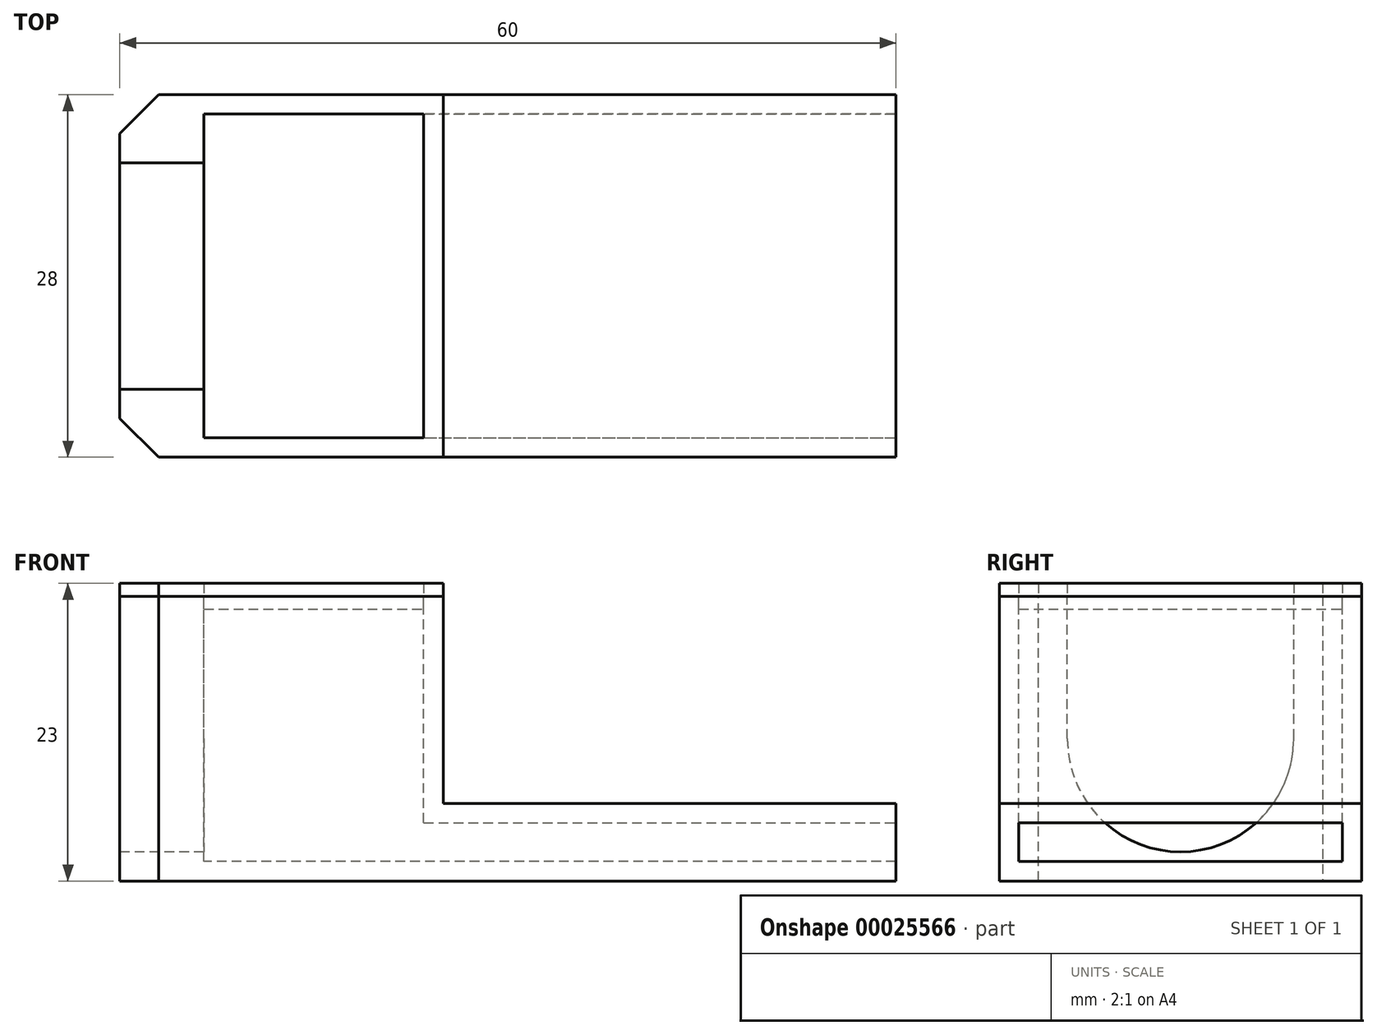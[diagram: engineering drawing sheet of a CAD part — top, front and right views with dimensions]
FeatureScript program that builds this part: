
annotation { "Feature Type Name" : "Feature", "Feature Type Description" : "" }
export const myFeature = defineFeature(function(context is Context, id is Id, definition is map)
    precondition{}
    {
        {
            var Q0;
            Q0=qCreatedBy(makeId("Front.planeOp"),FACE);
            var sketch = newSketch(context, id + "F0", { "sketchPlane" : qUnion([Q0])});
            skLineSegment(sketch, "E0", {"start": v(0, 0) * mm, "end": v(55, 0) * mm});
            skLineSegment(sketch, "E1", {"start": v(0, 0) * mm, "end": v(0, 22) * mm});
            skLineSegment(sketch, "E2", {"start": v(0, 22) * mm, "end": v(20, 22) * mm});
            skLineSegment(sketch, "E3", {"start": v(20, 22) * mm, "end": v(20, 6) * mm});
            skLineSegment(sketch, "E4", {"start": v(20, 6) * mm, "end": v(55, 6) * mm});
            skLineSegment(sketch, "E5", {"start": v(55, 6) * mm, "end": v(55, 0) * mm});
            skSolve(sketch);
        }
        {
            var Q0;
            Q0 = qSketchRegion(id + "F0", true);
            extrude(context, id + "F1", {"entities" : qUnion([Q0]), "depth" : 28 * mm});
        }
        {
            var Q0;
            Q0=makeQuery(id+"F1.opExtrude","SWEPT_FACE",FACE,{"disambiguationData":[OSD([sQuery(id+"F0.wireOp",EDGE,"E1")])]});
            var sketch = newSketch(context, id + "F2", { "sketchPlane" : qUnion([Q0])});
            skArc(sketch, "E6", {"start": v(5.25, 11) * mm, "mid": v(14, 2.25) * mm, "end": v(22.75, 11) * mm});
            skPoint(sketch, "E6.centerSnap0", {"position": v(28, 11) * mm});
            skPoint(sketch, "E6.centerSnap1", {"position": v(14, 22) * mm});
            skLineSegment(sketch, "E7", {"start": v(5.25, 11) * mm, "end": v(5.25, 22) * mm});
            skLineSegment(sketch, "E8", {"start": v(22.75, 11) * mm, "end": v(22.75, 22) * mm});
            skSolve(sketch);
        }
        {
            var Q0;
            Q0=makeQuery(id+"F1.opExtrude","SWEPT_FACE",FACE,{"disambiguationData":[OSD([sQuery(id+"F0.wireOp",EDGE,"E2")])]});
            var sketch = newSketch(context, id + "F3", { "sketchPlane" : qUnion([Q0])});
            skLineSegment(sketch, "E9.0", {"start": v(18.5, -1.5) * mm, "end": v(1.5, -1.5) * mm});
            skLineSegment(sketch, "E9.1", {"start": v(18.5, -26.5) * mm, "end": v(18.5, -1.5) * mm});
            skLineSegment(sketch, "E9.2", {"start": v(1.5, -26.5) * mm, "end": v(18.5, -26.5) * mm});
            skLineSegment(sketch, "E9.3", {"start": v(1.5, -1.5) * mm, "end": v(1.5, -26.5) * mm});
            skSolve(sketch);
        }
        {
            var Q0;
            Q0=makeQuery(id+"F3.imprint","IMPRINT",FACE,{"disambiguationData":[TD([[makeQuery(id+"F3.imprint","IMPRINT",EDGE,{"derivedFrom":sQuery(id+"F3.wireOp",EDGE,"E9.0")}),1.0]])]});
            extrude(context, id + "F4", {"entities" : qUnion([Q0]), "operationType" : NewBodyOperationType.REMOVE, "oppositeDirection" : true, "depth" : 20.5 * mm});
        }
        {
            var Q0;
            Q0 = qSketchRegion(id + "F2", true);
            var Q1;
            Q1=makeQuery(id+"F2.imprint","IMPRINT",FACE,{"disambiguationData":[TD([[makeQuery(id+"F2.imprint","IMPRINT",EDGE,{"derivedFrom":sQuery(id+"F2.wireOp",EDGE,"E6")}),1.0]])]});
            extrude(context, id + "F5", {"entities" : qUnion([Q0, Q1]), "operationType" : NewBodyOperationType.REMOVE, "oppositeDirection" : true, "depth" : 2 * mm});
        }
        {
            var Q0;
            Q0=makeQuery(id+"F1.opExtrude","SWEPT_FACE",FACE,{"disambiguationData":[OSD([sQuery(id+"F0.wireOp",EDGE,"E5")])]});
            var sketch = newSketch(context, id + "F6", { "sketchPlane" : qUnion([Q0])});
            skLineSegment(sketch, "E10.0", {"start": v(-1.5, 1.5) * mm, "end": v(-1.5, 4.5) * mm});
            skLineSegment(sketch, "E10.1", {"start": v(-26.5, 1.5) * mm, "end": v(-1.5, 1.5) * mm});
            skLineSegment(sketch, "E10.2", {"start": v(-26.5, 4.5) * mm, "end": v(-26.5, 1.5) * mm});
            skLineSegment(sketch, "E10.3", {"start": v(-1.5, 4.5) * mm, "end": v(-26.5, 4.5) * mm});
            skSolve(sketch);
        }
        {
            var Q0;
            Q0=makeQuery(id+"F6.imprint","IMPRINT",FACE,{"disambiguationData":[TD([[makeQuery(id+"F6.imprint","IMPRINT",EDGE,{"derivedFrom":sQuery(id+"F6.wireOp",EDGE,"E10.0")}),1.0]])]});
            extrude(context, id + "F7", {"entities" : qUnion([Q0]), "operationType" : NewBodyOperationType.REMOVE, "oppositeDirection" : true, "depth" : 40 * mm});
        }
        {
            var Q0;
            Q0=makeQuery(id+"F1.opExtrude","SWEPT_FACE",FACE,{"disambiguationData":[OSD([sQuery(id+"F0.wireOp",EDGE,"E1")])]});
            extrude(context, id + "F8", {"entities" : qUnion([Q0]), "operationType" : NewBodyOperationType.ADD, "depth" : 5 * mm});
        }
        {
            var Q0;
            {var subQ0=sQuery(id+"F0.wireOp",EDGE,"E1");Q0=makeQuery(id+"F8.opExtrude","CAP_EDGE",EDGE,{"disambiguationData":[OSD([subQ0]),TDD([makeQuery(id+"F1.opExtrude","CAP_EDGE",EDGE,{"disambiguationData":[OSD([subQ0])],"isStart":false})])],"isStart":false});}
            var Q1;
            {var subQ0=sQuery(id+"F0.wireOp",EDGE,"E1");Q1=makeQuery(id+"F8.opExtrude","CAP_EDGE",EDGE,{"disambiguationData":[OSD([subQ0]),TDD([makeQuery(id+"F1.opExtrude","CAP_EDGE",EDGE,{"disambiguationData":[OSD([subQ0])],"isStart":true})])],"isStart":false});}
            chamfer(context, id + "F9", {"entities" : qUnion([Q0, Q1]), "width" : 3 * mm, "tangentPropagation" : true});
        }
        {
            var Q0;
            {var subQ0=sQuery(id+"F0.wireOp",EDGE,"E2");var subQ1=makeQuery(id+"F1.opExtrude","SWEPT_FACE",FACE,{"disambiguationData":[OSD([subQ0])]});var subQ2=sQuery(id+"F0.wireOp",EDGE,"E1");var subQ3=makeQuery(id+"F1.opExtrude","SWEPT_EDGE",EDGE,{"disambiguationData":[OSD([subQ2,subQ0])]});Q0=makeQuery(id+"F8.boolean.opBoolean","MERGE",FACE,{"derivedFrom":[subQ1,makeQuery(id+"F8.opExtrude","SWEPT_FACE",FACE,{"disambiguationData":[OSD([subQ2,subQ0]),TDD([makeQuery(id+"F5.boolean.opBoolean","SPLIT",EDGE,{"disambiguationData":[TD([makeQuery(id+"F5.opExtrude","SWEPT_FACE",FACE,{"disambiguationData":[OSD([sQuery(id+"F2.wireOp",EDGE,"E7")])]})])],"derivedFrom":subQ3})])]}),makeQuery(id+"F8.opExtrude","SWEPT_FACE",FACE,{"disambiguationData":[OSD([subQ2,subQ0]),TDD([makeQuery(id+"F5.boolean.opBoolean","SPLIT",EDGE,{"disambiguationData":[TD([makeQuery(id+"F5.opExtrude","SWEPT_FACE",FACE,{"disambiguationData":[OSD([sQuery(id+"F2.wireOp",EDGE,"E8")])]})])],"derivedFrom":subQ3})])]})]});}
            var sketch = newSketch(context, id + "F10", { "sketchPlane" : qUnion([Q0])});
            skLineSegment(sketch, "E11", {"start": v(-5, -3) * mm, "end": v(-2, 0) * mm});
            skLineSegment(sketch, "E12", {"start": v(-2, 0) * mm, "end": v(20, 0) * mm});
            skLineSegment(sketch, "E13", {"start": v(20, 0) * mm, "end": v(20, -28) * mm});
            skLineSegment(sketch, "E14", {"start": v(-2, -28) * mm, "end": v(-5, -25) * mm});
            skLineSegment(sketch, "E15", {"start": v(-5, -25) * mm, "end": v(-5, -3) * mm});
            skLineSegment(sketch, "E16", {"start": v(1.5, -5.25) * mm, "end": v(1.5, -1.5) * mm});
            skLineSegment(sketch, "E17", {"start": v(1.5, -1.5) * mm, "end": v(18.5, -1.5) * mm});
            skLineSegment(sketch, "E18", {"start": v(18.5, -1.5) * mm, "end": v(18.5, -26.5) * mm});
            skLineSegment(sketch, "E19", {"start": v(18.5, -26.5) * mm, "end": v(1.5, -26.5) * mm});
            skLineSegment(sketch, "E20", {"start": v(1.5, -26.5) * mm, "end": v(1.5, -1.5) * mm});
            skSolve(sketch);
        }
        {
            var Q0;
            {var subQ8=sQuery(id+"F10.wireOp",EDGE,"E17");Q0=makeQuery(id+"F10.imprint","IMPRINT",FACE,{"disambiguationData":[TD([[makeQuery(id+"F10.imprint","IMPRINT",EDGE,{"derivedFrom":subQ8}),1.0]])]});}
            extrude(context, id + "F11", {"entities" : qUnion([Q0]), "oppositeDirection" : true, "depth" : 1 * mm});
        }
        {
            var Q0;
            {var subQ0=sQuery(id+"F0.wireOp",EDGE,"E2");var subQ1=makeQuery(id+"F1.opExtrude","SWEPT_FACE",FACE,{"disambiguationData":[OSD([subQ0])]});var subQ2=sQuery(id+"F0.wireOp",EDGE,"E1");var subQ3=makeQuery(id+"F1.opExtrude","SWEPT_EDGE",EDGE,{"disambiguationData":[OSD([subQ2,subQ0])]});Q0=makeQuery(id+"F8.boolean.opBoolean","MERGE",FACE,{"derivedFrom":[subQ1,makeQuery(id+"F8.opExtrude","SWEPT_FACE",FACE,{"disambiguationData":[OSD([subQ2,subQ0]),TDD([makeQuery(id+"F5.boolean.opBoolean","SPLIT",EDGE,{"disambiguationData":[TD([makeQuery(id+"F5.opExtrude","SWEPT_FACE",FACE,{"disambiguationData":[OSD([sQuery(id+"F2.wireOp",EDGE,"E7")])]})])],"derivedFrom":subQ3})])]}),makeQuery(id+"F8.opExtrude","SWEPT_FACE",FACE,{"disambiguationData":[OSD([subQ2,subQ0]),TDD([makeQuery(id+"F5.boolean.opBoolean","SPLIT",EDGE,{"disambiguationData":[TD([makeQuery(id+"F5.opExtrude","SWEPT_FACE",FACE,{"disambiguationData":[OSD([sQuery(id+"F2.wireOp",EDGE,"E8")])]})])],"derivedFrom":subQ3})])]})]});}
            var Q1;
            Q1=makeQuery(id+"F11.opExtrude","CAP_FACE",FACE,{"disambiguationData":[OSD([sQuery(id+"F10.wireOp",EDGE,"E17"),sQuery(id+"F10.wireOp",EDGE,"E18"),sQuery(id+"F10.wireOp",EDGE,"E19"),sQuery(id+"F10.wireOp",EDGE,"E20")])],"isStart":true});
            var Q2;
            {var subQ0=sQuery(id+"F0.wireOp",EDGE,"E1");var subQ1=sQuery(id+"F0.wireOp",EDGE,"E2");var subQ4=sQuery(id+"F2.wireOp",EDGE,"E7");var subQ5=makeQuery(id+"F8.boolean.opBoolean","MERGE",EDGE,{"derivedFrom":[makeQuery(id+"F5.boolean.opBoolean","COPY",EDGE,{"derivedFrom":makeQuery(id+"F5.opExtrude","SWEPT_EDGE",EDGE,{"disambiguationData":[OSD([subQ0,subQ1,subQ4])]})}),makeQuery(id+"F8.opExtrude","SWEPT_EDGE",EDGE,{"disambiguationData":[OSD([subQ0,subQ1,subQ4])]})]});Q2=makeQuery(id+"F10.imprint","IMPRINT",FACE,{"disambiguationData":[TD([[makeQuery(id+"F10.imprint","IMPRINT",EDGE,{"derivedFrom":subQ5}),1.0]])]});}
            extrude(context, id + "F12", {"entities" : qUnion([Q0, Q1, Q2]), "depth" : 1 * mm});
        }
    });
